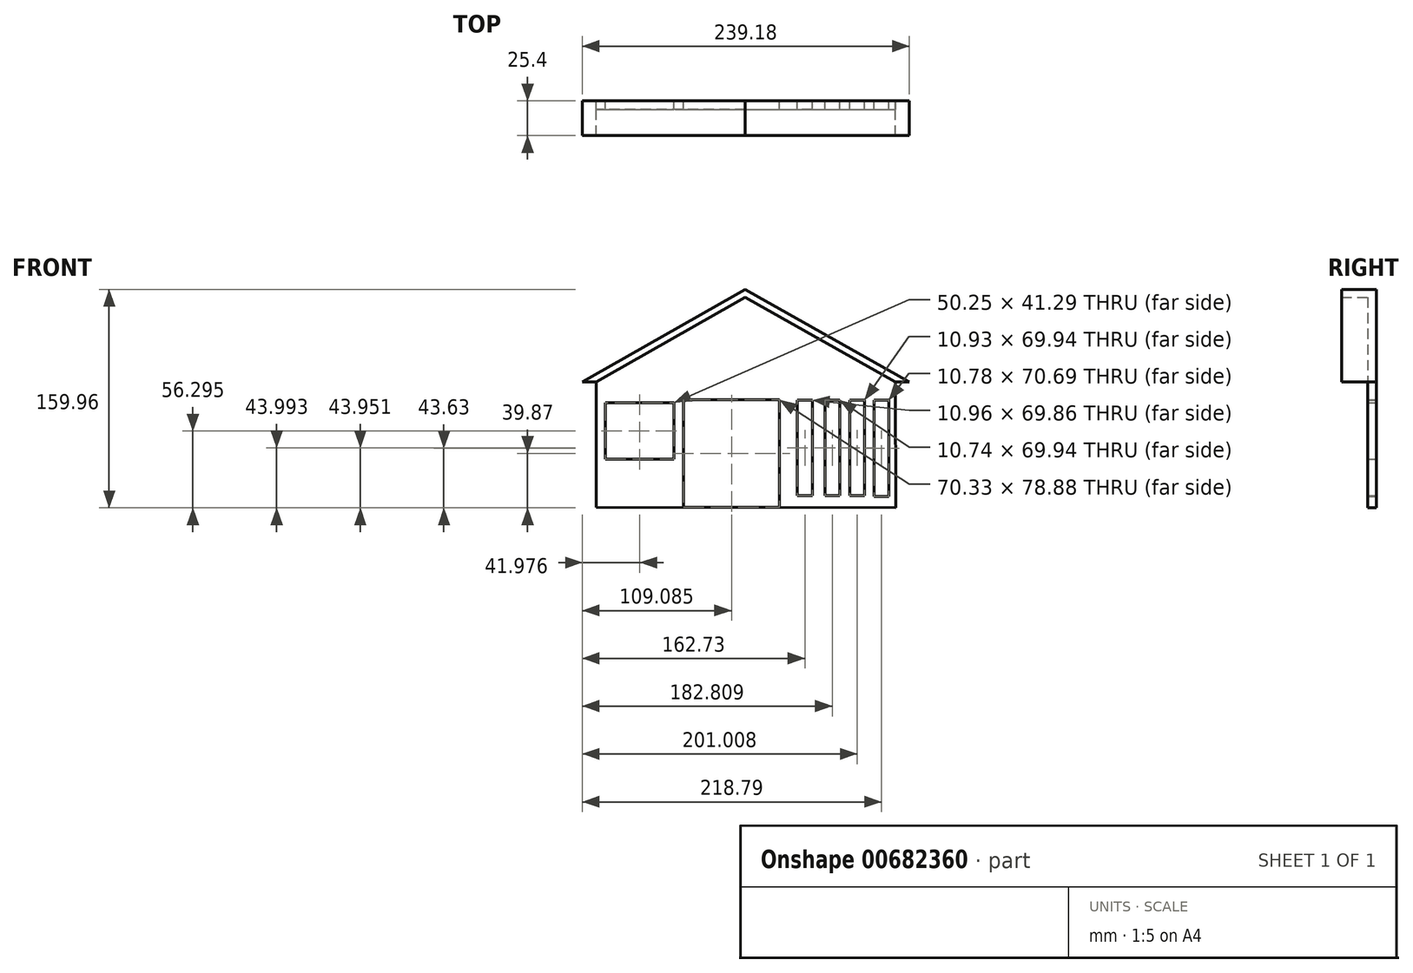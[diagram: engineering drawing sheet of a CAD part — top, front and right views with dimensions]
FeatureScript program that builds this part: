
annotation { "Feature Type Name" : "Feature", "Feature Type Description" : "" }
export const myFeature = defineFeature(function(context is Context, id is Id, definition is map)
    precondition{}
    {
        {
            var Q0;
            Q0=qCreatedBy(makeId("Front.planeOp"),FACE);
            var sketch = newSketch(context, id + "F0", { "sketchPlane" : qUnion([Q0])});
            skLineSegment(sketch, "E0", {"start": v(0, 124.31) * mm, "end": v(-119.15, 56.65) * mm});
            skLineSegment(sketch, "E1", {"start": v(120.03, 56.65) * mm, "end": v(0, 124.31) * mm});
            skLineSegment(sketch, "E2.bottom", {"start": v(-102.3, 41.29) * mm, "end": v(-52.05, 41.29) * mm});
            skLineSegment(sketch, "E2.top", {"start": v(-102.3, 0) * mm, "end": v(-52.05, 0) * mm});
            skLineSegment(sketch, "E2.left", {"start": v(-102.3, 41.29) * mm, "end": v(-102.3, 0) * mm});
            skLineSegment(sketch, "E2.right", {"start": v(-52.05, 41.29) * mm, "end": v(-52.05, 0) * mm});
            skLineSegment(sketch, "E3.bottom", {"start": v(58.3, -26.67) * mm, "end": v(69.03, -26.67) * mm});
            skLineSegment(sketch, "E3.top", {"start": v(58.3, -26.67) * mm, "end": v(69.03, -26.67) * mm});
            skLineSegment(sketch, "E3.left", {"start": v(69.03, -26.67) * mm, "end": v(69.03, -26.67) * mm});
            skLineSegment(sketch, "E3.right", {"start": v(58.3, -26.67) * mm, "end": v(58.3, -26.67) * mm});
            skLineSegment(sketch, "E4.bottom", {"start": v(76.4, 43.27) * mm, "end": v(87.32, 43.27) * mm});
            skLineSegment(sketch, "E4.top", {"start": v(76.4, -26.67) * mm, "end": v(87.32, -26.67) * mm});
            skLineSegment(sketch, "E4.left", {"start": v(76.4, 43.27) * mm, "end": v(76.4, -26.67) * mm});
            skLineSegment(sketch, "E4.right", {"start": v(87.32, 43.27) * mm, "end": v(87.32, -26.67) * mm});
            skLineSegment(sketch, "E5", {"start": v(69.03, -26.67) * mm, "end": v(69.03, 43.27) * mm});
            skLineSegment(sketch, "E6", {"start": v(58.3, -26.67) * mm, "end": v(58.3, 43.27) * mm});
            skLineSegment(sketch, "E7.bottom", {"start": v(-45.23, 43.66) * mm, "end": v(25.1, 43.66) * mm});
            skLineSegment(sketch, "E7.top", {"start": v(-45.23, -35.22) * mm, "end": v(25.1, -35.22) * mm});
            skLineSegment(sketch, "E7.left", {"start": v(-45.23, 43.66) * mm, "end": v(-45.23, -35.22) * mm});
            skLineSegment(sketch, "E7.right", {"start": v(25.1, 43.66) * mm, "end": v(25.1, -35.22) * mm});
            skLineSegment(sketch, "E8", {"start": v(-10.07, 43.66) * mm, "end": v(-10.07, -35.22) * mm});
            skLineSegment(sketch, "E9.bottom", {"start": v(49.06, 43.27) * mm, "end": v(38.1, 43.27) * mm});
            skLineSegment(sketch, "E9.left", {"start": v(49.06, 43.27) * mm, "end": v(49.06, -26.58) * mm});
            skLineSegment(sketch, "E9.right", {"start": v(38.1, 43.27) * mm, "end": v(38.1, -26.58) * mm});
            skLineSegment(sketch, "E10", {"start": v(-45.23, -33.44) * mm, "end": v(25.1, -33.44) * mm});
            skPoint(sketch, "E11.firstSnap0", {"position": v(25.1, 4.22) * mm});
            skLineSegment(sketch, "E11.left", {"start": v(25.1, 0) * mm, "end": v(25.1, -35.65) * mm});
            skLineSegment(sketch, "E12.bottom", {"start": v(94.25, 43.33) * mm, "end": v(105.03, 43.33) * mm});
            skLineSegment(sketch, "E12.top", {"start": v(94.25, -27.36) * mm, "end": v(105.03, -27.36) * mm});
            skLineSegment(sketch, "E12.left", {"start": v(94.25, 43.33) * mm, "end": v(94.25, -27.36) * mm});
            skLineSegment(sketch, "E12.right", {"start": v(105.03, 43.33) * mm, "end": v(105.03, -27.36) * mm});
            skLineSegment(sketch, "E13", {"start": v(0, 118.49) * mm, "end": v(-108.89, 56.65) * mm});
            skLineSegment(sketch, "E14", {"start": v(0, 118.49) * mm, "end": v(109.7, 56.65) * mm});
            skLineSegment(sketch, "E15", {"start": v(-108.89, 56.65) * mm, "end": v(-108.89, -35.22) * mm});
            skLineSegment(sketch, "E16", {"start": v(-119.15, 56.65) * mm, "end": v(-108.89, 56.65) * mm});
            skLineSegment(sketch, "E17", {"start": v(109.7, 56.65) * mm, "end": v(109.9, -35.65) * mm});
            skLineSegment(sketch, "E18", {"start": v(109.7, 56.65) * mm, "end": v(120.03, 56.65) * mm});
            skLineSegment(sketch, "E19", {"start": v(38.1, -26.58) * mm, "end": v(49.06, -26.58) * mm});
            skLineSegment(sketch, "E20", {"start": v(-108.89, -35.22) * mm, "end": v(109.9, -35.65) * mm});
            skLineSegment(sketch, "E21", {"start": v(58.3, 43.27) * mm, "end": v(69.03, 43.27) * mm});
            skSolve(sketch);
        }
        {
            var Q0;
            Q0=makeQuery(id+"F0.imprint","IMPRINT",FACE,{"disambiguationData":[TD([[makeQuery(id+"F0.imprint","IMPRINT",EDGE,{"derivedFrom":sQuery(id+"F0.wireOp",EDGE,"E0")}),1.0]])]});
            extrude(context, id + "F1", {"entities" : qUnion([Q0]), "depth" : 25.4 * mm, "offsetDistance" : 25.4 * mm});
        }
        {
            var Q0;
            Q0 = qSketchRegion(id + "F0", true);
            extrude(context, id + "F2", {"entities" : qUnion([Q0]), "operationType" : NewBodyOperationType.ADD, "depth" : 6.35 * mm, "offsetDistance" : 25.4 * mm});
        }
    });
